# Revit family: Aero
name_source: partatom
category: Mechanical Equipment
units: mm (PartAtom-declared; Revit-internal decimal feet)

## family parameters
Always vertical = Yes
Classification = None
Cut with Voids When Loaded = No
Part Type = Normal
Room Calculation Point = No
Round Connector Dimension = Use Diameter
Shared = No
Work Plane-Based = No

## types (12) — shared parameters
00_20_Manufacturer = Blauberg
00_20_Name = Extraction fan
Amperage = 0 A
Description = For round channels
Frequency = 50 Hz
Load Classification = HVAC
Maintenance zone material = <By Category>
Manufacturer = Blauberg
Number of Fase = 1
URL = https://blaubergventilatoren.de
Voltage = 230 V
e = 30 mm  [stored 0.0984252 ft]
zero-valued in all types: Default Elevation

## per-type parameters (varying)
| type | Apparent Load | Casing Material | Diameter | Dy | H | Height | L2 | Length | Maximum Air Flow | Panel | Power | Sound pressure level at 3 m distance | Weight | Width | a | c | d |
| Aero 150 Chrome | 30 W | Plastic, opaque, Chrome | 150 mm | 145 mm  [stored 0.475722 ft] | 198 mm  [stored 0.649606 ft] | 198 mm  [stored 0.649606 ft] | 89 mm  [stored 0.291995 ft] | 119 mm  [stored 0.39042 ft] | 309.0 m³/h | Panel : Chrome | 24 W | 40 dBA | 0.89 kg | 198 mm  [stored 0.649606 ft] | 198 mm  [stored 0.649606 ft] | 119 mm  [stored 0.39042 ft] | 150 mm |
| Aero 100 Chrome | 21 W | Plastic, opaque, Chrome | 100 mm  [stored 0.328084 ft] | 95 mm | 144 mm  [stored 0.472441 ft] | 144 mm  [stored 0.472441 ft] | 63 mm  [stored 0.206693 ft] | 93 mm | 102.0 m³/h | Panel : Chrome | 14 W | 38 dBA | 0.55 kg | 144 mm  [stored 0.472441 ft] | 144 mm  [stored 0.472441 ft] | 93 mm | 100 mm  [stored 0.328084 ft] |
| Aero 125 Chrome | 23 W | Plastic, opaque, Chrome | 125 mm  [stored 0.410105 ft] | 120 mm  [stored 0.393701 ft] | 168 mm  [stored 0.551181 ft] | 168 mm  [stored 0.551181 ft] | 67 mm | 97 mm  [stored 0.318241 ft] | 193.0 m³/h | Panel : Chrome | 16 W | 39 dBA | 0.70 kg | 168 mm  [stored 0.551181 ft] | 168 mm  [stored 0.551181 ft] | 97 mm  [stored 0.318241 ft] | 125 mm  [stored 0.410105 ft] |
| Aero 150 Gold | 30 W | Plastic, opaque, Gold | 150 mm | 145 mm  [stored 0.475722 ft] | 198 mm  [stored 0.649606 ft] | 198 mm  [stored 0.649606 ft] | 89 mm  [stored 0.291995 ft] | 119 mm  [stored 0.39042 ft] | 309.0 m³/h | Panel : Gold | 24 W | 40 dBA | 0.89 kg | 198 mm  [stored 0.649606 ft] | 198 mm  [stored 0.649606 ft] | 119 mm  [stored 0.39042 ft] | 150 mm |
| Aero 125 Gold | 23 W | Plastic, opaque, Gold | 125 mm  [stored 0.410105 ft] | 120 mm  [stored 0.393701 ft] | 168 mm  [stored 0.551181 ft] | 168 mm  [stored 0.551181 ft] | 67 mm | 97 mm  [stored 0.318241 ft] | 193.0 m³/h | Panel : Gold | 16 W | 39 dBA | 0.70 kg | 168 mm  [stored 0.551181 ft] | 168 mm  [stored 0.551181 ft] | 97 mm  [stored 0.318241 ft] | 125 mm  [stored 0.410105 ft] |
| Aero 100 Gold | 21 W | Plastic, opaque, Gold | 100 mm  [stored 0.328084 ft] | 95 mm | 144 mm  [stored 0.472441 ft] | 144 mm  [stored 0.472441 ft] | 63 mm  [stored 0.206693 ft] | 93 mm | 102.0 m³/h | Panel : Gold | 14 W | 38 dBA | 0.55 kg | 144 mm  [stored 0.472441 ft] | 144 mm  [stored 0.472441 ft] | 93 mm | 100 mm  [stored 0.328084 ft] |
| Aero 100 Vintage | 21 W | Plastic, opaque, Vintage | 100 mm  [stored 0.328084 ft] | 95 mm | 144 mm  [stored 0.472441 ft] | 144 mm  [stored 0.472441 ft] | 63 mm  [stored 0.206693 ft] | 93 mm | 102.0 m³/h | Panel : Vintage | 14 W | 38 dBA | 0.55 kg | 144 mm  [stored 0.472441 ft] | 144 mm  [stored 0.472441 ft] | 93 mm | 100 mm  [stored 0.328084 ft] |
| Aero 125 Vintage | 23 W | Plastic, opaque, Vintage | 125 mm  [stored 0.410105 ft] | 120 mm  [stored 0.393701 ft] | 168 mm  [stored 0.551181 ft] | 168 mm  [stored 0.551181 ft] | 67 mm | 97 mm  [stored 0.318241 ft] | 193.0 m³/h | Panel : Vintage | 16 W | 39 dBA | 0.70 kg | 168 mm  [stored 0.551181 ft] | 168 mm  [stored 0.551181 ft] | 97 mm  [stored 0.318241 ft] | 125 mm  [stored 0.410105 ft] |
| Aero 150 Vintage | 30 W | Plastic, opaque, Vintage | 150 mm | 145 mm  [stored 0.475722 ft] | 198 mm  [stored 0.649606 ft] | 198 mm  [stored 0.649606 ft] | 89 mm  [stored 0.291995 ft] | 119 mm  [stored 0.39042 ft] | 309.0 m³/h | Panel : Vintage | 24 W | 40 dBA | 0.89 kg | 198 mm  [stored 0.649606 ft] | 198 mm  [stored 0.649606 ft] | 119 mm  [stored 0.39042 ft] | 150 mm |
| Aero 150 Wite | 30 W | Plastic, opaque, white | 150 mm | 145 mm  [stored 0.475722 ft] | 198 mm  [stored 0.649606 ft] | 198 mm  [stored 0.649606 ft] | 89 mm  [stored 0.291995 ft] | 119 mm  [stored 0.39042 ft] | 309.0 m³/h | Panel : White | 24 W | 40 dBA | 0.89 kg | 198 mm  [stored 0.649606 ft] | 198 mm  [stored 0.649606 ft] | 119 mm  [stored 0.39042 ft] | 150 mm |
| Aero 125 Wite | 23 W | Plastic, opaque, white | 125 mm  [stored 0.410105 ft] | 120 mm  [stored 0.393701 ft] | 168 mm  [stored 0.551181 ft] | 168 mm  [stored 0.551181 ft] | 67 mm | 97 mm  [stored 0.318241 ft] | 193.0 m³/h | Panel : White | 16 W | 39 dBA | 0.70 kg | 168 mm  [stored 0.551181 ft] | 168 mm  [stored 0.551181 ft] | 97 mm  [stored 0.318241 ft] | 125 mm  [stored 0.410105 ft] |
| Aero 100 Wite | 21 W | Plastic, opaque, white | 100 mm  [stored 0.328084 ft] | 95 mm | 144 mm  [stored 0.472441 ft] | 144 mm  [stored 0.472441 ft] | 63 mm  [stored 0.206693 ft] | 93 mm | 102.0 m³/h | Panel : White | 14 W | 38 dBA | 0.55 kg | 144 mm  [stored 0.472441 ft] | 144 mm  [stored 0.472441 ft] | 93 mm | 100 mm  [stored 0.328084 ft] |

note: column(s) folded — value = type name in every type: 00_20_Type

note: [stored X ft] marks values corroborated as IEEE doubles in the binary element streams (Revit-internal decimal feet)
